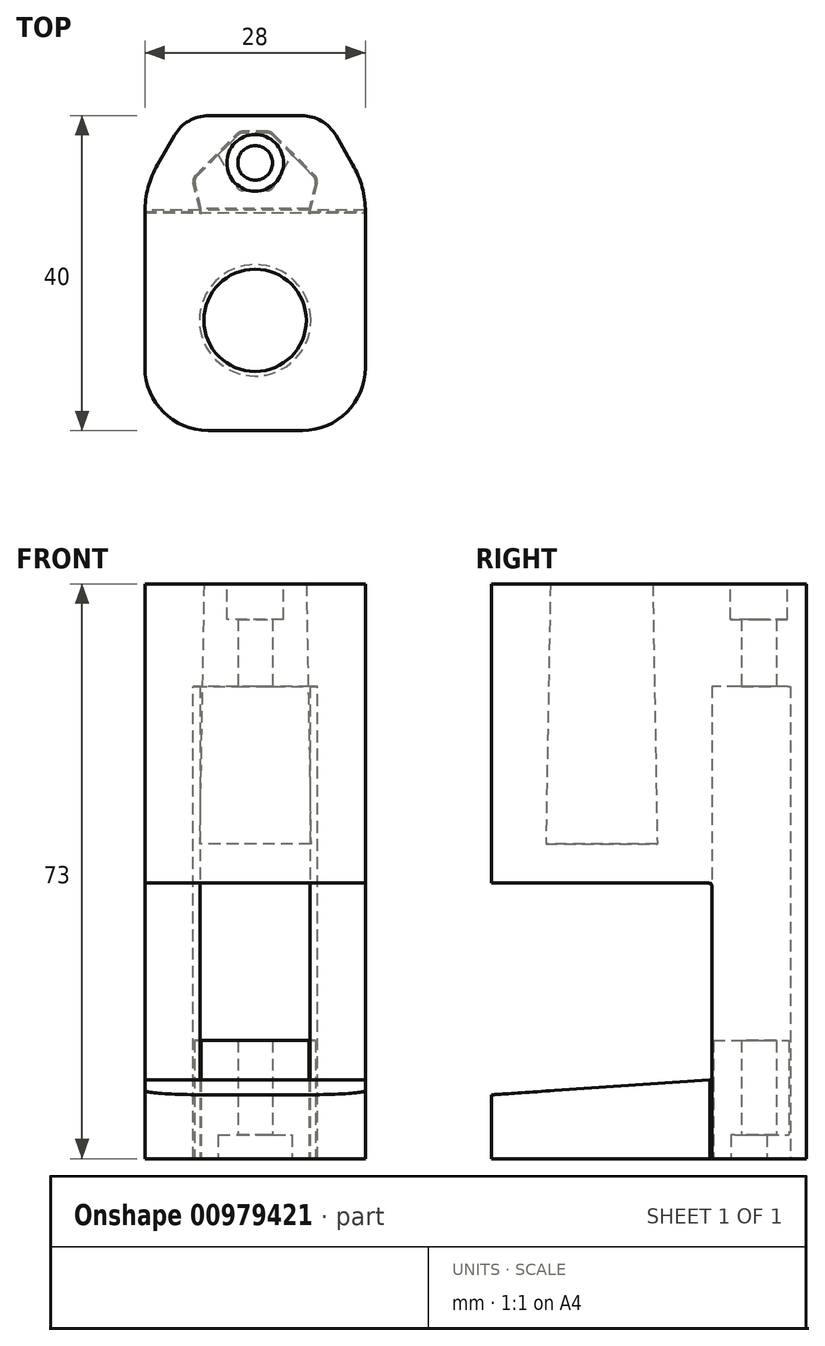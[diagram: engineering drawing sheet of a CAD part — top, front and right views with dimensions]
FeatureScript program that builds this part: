
annotation { "Feature Type Name" : "Feature", "Feature Type Description" : "" }
export const myFeature = defineFeature(function(context is Context, id is Id, definition is map)
    precondition{}
    {
        {
            assignVariable(context, id + "F0", {"name" : "lamppostDepth", "anyValue" : 33});
        }
        {
            var Q0;
            Q0=qCreatedBy(makeId("Right.planeOp"),FACE);
            var sketch = newSketch(context, id + "F1", { "sketchPlane" : qUnion([Q0])});
            skLineSegment(sketch, "E0", {"start": v(0, 0) * mm, "end": v(-28, 0) * mm});
            skLineSegment(sketch, "E1", {"start": v(-28, 0) * mm, "end": v(-28, 38) * mm});
            skLineSegment(sketch, "E2", {"start": v(-28, 38) * mm, "end": v(12, 38) * mm});
            skLineSegment(sketch, "E3", {"start": v(12, 38) * mm, "end": v(12, -35) * mm});
            skLineSegment(sketch, "E4", {"start": v(12, -35) * mm, "end": v(0, -35) * mm});
            skLineSegment(sketch, "E5", {"start": v(0, -35) * mm, "end": v(0, 0) * mm});
            skLineSegment(sketch, "E6", {"start": v(0, -25) * mm, "end": v(-22.92, -25) * mm, "construction": true});
            skSolve(sketch);
        }
        {
            var Q0;
            Q0=qSketchRegion(id+"F1",true);
            extrude(context, id + "F2", {"entities" : qUnion([Q0]), "endBound" : BoundingType.SYMMETRIC, "depth" : 28 * mm, "offsetDistance" : 25 * mm});
        }
        {
            var Q0;
            Q0=makeQuery(id+"F2.opExtrude","SWEPT_FACE",FACE,{"disambiguationData":[OSD([sQuery(id+"F1.wireOp",EDGE,"E2")])]});
            var sketch = newSketch(context, id + "F3", { "sketchPlane" : qUnion([Q0])});
            skCircle(sketch, "E7", {"center": v(0, -14) * mm, "radius": 6.5 * mm});
            skLineSegment(sketch, "E8", {"start": v(14, -28) * mm, "end": v(-14, 0) * mm, "construction": true});
            skLineSegment(sketch, "E9", {"start": v(-14, 0) * mm, "end": v(-14, -28) * mm, "construction": true});
            skSolve(sketch);
        }
        {
            var Q0;
            Q0=qSketchRegion(id+"F3",true);
            extrude(context, id + "F4", {"entities" : qUnion([Q0]), "operationType" : NewBodyOperationType.REMOVE, "oppositeDirection" : true, "depth" : (getVariable(context, 'lamppostDepth')) * mm, "offsetDistance" : 25 * mm, "hasDraft" : true, "draftAngle" : 1 * degree});
        }
        {
            var Q0;
            Q0=makeQuery(id+"F2.opExtrude","SWEPT_FACE",FACE,{"disambiguationData":[OSD([sQuery(id+"F1.wireOp",EDGE,"E4")])]});
            var sketch = newSketch(context, id + "F5", { "sketchPlane" : qUnion([Q0])});
            skCircle(sketch, "E10", {"center": v(0, -6) * mm, "radius": 2.2 * mm});
            skLineSegment(sketch, "E11", {"start": v(-14, -12) * mm, "end": v(14, 0) * mm, "construction": true});
            skSolve(sketch);
        }
        {
            var Q0;
            Q0=qSketchRegion(id+"F5",true);
            extrude(context, id + "F6", {"entities" : qUnion([Q0]), "operationType" : NewBodyOperationType.REMOVE, "endBound" : BoundingType.THROUGH_ALL, "oppositeDirection" : true, "depth" : 25 * mm, "offsetDistance" : 25 * mm});
        }
        {
            var Q0;
            Q0=makeQuery(id+"F2.opExtrude","SWEPT_FACE",FACE,{"disambiguationData":[OSD([sQuery(id+"F1.wireOp",EDGE,"E2")])]});
            var sketch = newSketch(context, id + "F7", { "sketchPlane" : qUnion([Q0])});
            skCircle(sketch, "E12", {"center": v(0, 6) * mm, "radius": 3.6 * mm});
            skSolve(sketch);
        }
        {
            var Q0;
            Q0=qSketchRegion(id+"F7",true);
            extrude(context, id + "F8", {"entities" : qUnion([Q0]), "operationType" : NewBodyOperationType.REMOVE, "oppositeDirection" : true, "depth" : 4.5 * mm, "offsetDistance" : 25 * mm});
        }
        {
            var Q0;
            Q0=makeQuery(id+"F2.opExtrude","SWEPT_FACE",FACE,{"disambiguationData":[OSD([sQuery(id+"F1.wireOp",EDGE,"E4")])]});
            var sketch = newSketch(context, id + "F9", { "sketchPlane" : qUnion([Q0])});
            skLineSegment(sketch, "E13", {"start": v(2, -10) * mm, "end": v(-2, -10) * mm});
            skPoint(sketch, "E14", {"position": v(0, -6) * mm});
            skLineSegment(sketch, "E15", {"start": v(0, -6) * mm, "end": v(0, -10) * mm, "construction": true});
            skLineSegment(sketch, "E16", {"start": v(2, -10) * mm, "end": v(8, -4) * mm});
            skLineSegment(sketch, "E17", {"start": v(8, -4) * mm, "end": v(7, 0) * mm});
            skLineSegment(sketch, "E18", {"start": v(7, 0) * mm, "end": v(-7, 0) * mm});
            skLineSegment(sketch, "E19", {"start": v(-7, 0) * mm, "end": v(-8, -4) * mm});
            skLineSegment(sketch, "E20", {"start": v(-8, -4) * mm, "end": v(-2, -10) * mm});
            skSolve(sketch);
        }
        {
            var Q0;
            Q0=qSketchRegion(id+"F9",true);
            extrude(context, id + "F10", {"entities" : qUnion([Q0]), "operationType" : NewBodyOperationType.REMOVE, "oppositeDirection" : true, "depth" : 60 * mm, "offsetDistance" : 25 * mm});
        }
        {
            var Q0;
            Q0=makeQuery(id+"F2.opExtrude","SWEPT_FACE",FACE,{"disambiguationData":[OSD([sQuery(id+"F1.wireOp",EDGE,"E4")])]});
            var sketch = newSketch(context, id + "F11", { "sketchPlane" : qUnion([Q0])});
            skLineSegment(sketch, "E21.0", {"start": v(7.78, -3.94) * mm, "end": v(6.84, -0.2) * mm});
            skLineSegment(sketch, "E21.1", {"start": v(-6.84, -0.2) * mm, "end": v(-7.78, -3.94) * mm});
            skLineSegment(sketch, "E21.2", {"start": v(-7.78, -3.94) * mm, "end": v(-1.92, -9.8) * mm});
            skLineSegment(sketch, "E21.3", {"start": v(1.92, -9.8) * mm, "end": v(-1.92, -9.8) * mm});
            skLineSegment(sketch, "E21.4", {"start": v(1.92, -9.8) * mm, "end": v(7.78, -3.94) * mm});
            skLineSegment(sketch, "E22", {"start": v(6.84, -0.2) * mm, "end": v(-6.84, -0.2) * mm});
            skCircle(sketch, "E23.0", {"center": v(0, -6) * mm, "radius": 2.2 * mm});
            skSolve(sketch);
        }
        {
            var Q0;
            Q0=qSketchRegion(id+"F11",true);
            extrude(context, id + "F12", {"entities" : qUnion([Q0]), "oppositeDirection" : true, "depth" : 15 * mm, "offsetDistance" : 25 * mm});
        }
        {
            var Q0;
            Q0=makeQuery(id+"F12.opExtrude","CAP_FACE",FACE,{"disambiguationData":[OSD([sQuery(id+"F11.wireOp",EDGE,"E21.0"),sQuery(id+"F11.wireOp",EDGE,"E21.1"),sQuery(id+"F11.wireOp",EDGE,"E21.2"),sQuery(id+"F11.wireOp",EDGE,"E21.3"),sQuery(id+"F11.wireOp",EDGE,"E21.4"),sQuery(id+"F11.wireOp",EDGE,"E22"),sQuery(id+"F11.wireOp",EDGE,"E23.0")])],"isStart":true});
            var sketch = newSketch(context, id + "F13", { "sketchPlane" : qUnion([Q0])});
            skLineSegment(sketch, "E24", {"start": v(14, 28) * mm, "end": v(-14, 28) * mm});
            skLineSegment(sketch, "E25", {"start": v(-14, 28) * mm, "end": v(-14, 0.2) * mm});
            skLineSegment(sketch, "E26", {"start": v(-14, 0.2) * mm, "end": v(-6.84, 0.2) * mm});
            skLineSegment(sketch, "E27", {"start": v(-6.84, 0.2) * mm, "end": v(-6.84, -0.2) * mm});
            skLineSegment(sketch, "E28", {"start": v(-6.84, -0.2) * mm, "end": v(6.84, -0.2) * mm});
            skLineSegment(sketch, "E29", {"start": v(6.84, -0.2) * mm, "end": v(6.84, 0.2) * mm});
            skLineSegment(sketch, "E30", {"start": v(6.84, 0.2) * mm, "end": v(14, 0.2) * mm});
            skLineSegment(sketch, "E31", {"start": v(14, 0.2) * mm, "end": v(14, 28) * mm});
            skSolve(sketch);
        }
        {
            var Q0;
            Q0=makeQuery(id+"F13.imprint","IMPRINT",FACE,{"disambiguationData":[TD([[makeQuery(id+"F13.imprint","IMPRINT",EDGE,{"derivedFrom":sQuery(id+"F13.wireOp",EDGE,"E24")}),1.0]])]});
            var Q1;
            Q1=sQuery(id+"F1.wireOp",VERTEX,"E6.end");
            extrude(context, id + "F14", {"entities" : qUnion([Q0]), "operationType" : NewBodyOperationType.ADD, "endBound" : BoundingType.UP_TO_VERTEX, "oppositeDirection" : true, "depth" : 10 * mm, "endBoundEntityVertex" : qUnion([Q1]), "offsetDistance" : 25 * mm});
        }
        {
            var Q0;
            Q0=makeQuery(id+"F14.boolean.opBoolean","MERGE",FACE,{"derivedFrom":[makeQuery(id+"F12.opExtrude","CAP_FACE",FACE,{"disambiguationData":[OSD([sQuery(id+"F11.wireOp",EDGE,"E21.0"),sQuery(id+"F11.wireOp",EDGE,"E21.1"),sQuery(id+"F11.wireOp",EDGE,"E21.2"),sQuery(id+"F11.wireOp",EDGE,"E21.3"),sQuery(id+"F11.wireOp",EDGE,"E21.4"),sQuery(id+"F11.wireOp",EDGE,"E22"),sQuery(id+"F11.wireOp",EDGE,"E23.0")])],"isStart":true}),makeQuery(id+"F14.opExtrude","CAP_FACE",FACE,{"disambiguationData":[OSD([sQuery(id+"F13.wireOp",EDGE,"E24"),sQuery(id+"F13.wireOp",EDGE,"E25"),sQuery(id+"F13.wireOp",EDGE,"E26"),sQuery(id+"F13.wireOp",EDGE,"E27"),sQuery(id+"F13.wireOp",EDGE,"E28"),sQuery(id+"F13.wireOp",EDGE,"E29"),sQuery(id+"F13.wireOp",EDGE,"E30"),sQuery(id+"F13.wireOp",EDGE,"E31")])],"isStart":true})]});
            var sketch = newSketch(context, id + "F15", { "sketchPlane" : qUnion([Q0])});
            skCircle(sketch, "E32", {"center": v(0, -6) * mm, "radius": 4.1 * mm, "construction": true});
            skLineSegment(sketch, "E33", {"start": v(2.05, -2.45) * mm, "end": v(-2.05, -2.45) * mm});
            skLineSegment(sketch, "E34", {"start": v(2.05, -2.45) * mm, "end": v(4.1, -6) * mm});
            skLineSegment(sketch, "E35", {"start": v(4.1, -6) * mm, "end": v(0, -6) * mm, "construction": true});
            skLineSegment(sketch, "E36", {"start": v(0, -6) * mm, "end": v(-4.1, -6) * mm, "construction": true});
            skLineSegment(sketch, "E37", {"start": v(-4.1, -6) * mm, "end": v(-2.05, -2.45) * mm});
            skLineSegment(sketch, "E38", {"start": v(4.1, -6) * mm, "end": v(4.7, -7.03) * mm});
            skLineSegment(sketch, "E39", {"start": v(4.7, -7.03) * mm, "end": v(1.92, -9.8) * mm});
            skLineSegment(sketch, "E40", {"start": v(1.92, -9.8) * mm, "end": v(-1.92, -9.8) * mm});
            skLineSegment(sketch, "E41", {"start": v(-1.92, -9.8) * mm, "end": v(-4.7, -7.03) * mm});
            skLineSegment(sketch, "E42", {"start": v(-4.7, -7.03) * mm, "end": v(-4.1, -6) * mm});
            skSolve(sketch);
        }
        {
            var Q0;
            Q0=qSketchRegion(id+"F15",true);
            extrude(context, id + "F16", {"entities" : qUnion([Q0]), "operationType" : NewBodyOperationType.REMOVE, "oppositeDirection" : true, "depth" : 3 * mm, "offsetDistance" : 25 * mm});
        }
        {
            var Q0;
            Q0=makeQuery(id+"F2.opExtrude","CAP_EDGE",EDGE,{"disambiguationData":[OSD([sQuery(id+"F1.wireOp",EDGE,"E1")])],"isStart":false});
            var Q1;
            Q1=makeQuery(id+"F2.opExtrude","CAP_EDGE",EDGE,{"disambiguationData":[OSD([sQuery(id+"F1.wireOp",EDGE,"E1")])],"isStart":true});
            var Q2;
            Q2=makeQuery(id+"F14.opExtrude","SWEPT_EDGE",EDGE,{"disambiguationData":[OSD([sQuery(id+"F13.wireOp",EDGE,"E24"),sQuery(id+"F13.wireOp",EDGE,"E31")])]});
            var Q3;
            Q3=makeQuery(id+"F14.opExtrude","SWEPT_EDGE",EDGE,{"disambiguationData":[OSD([sQuery(id+"F13.wireOp",EDGE,"E24"),sQuery(id+"F13.wireOp",EDGE,"E25")])]});
            fillet(context, id + "F17", {"entities" : qUnion([Q0, Q1, Q2, Q3]), "radius" : 8 * mm, "tangentPropagation" : true, "allowEdgeOverflow" : false});
        }
        {
            var Q0;
            Q0=makeQuery(id+"F2.opExtrude","CAP_EDGE",EDGE,{"disambiguationData":[OSD([sQuery(id+"F1.wireOp",EDGE,"E3")])],"isStart":true});
            var Q1;
            Q1=makeQuery(id+"F2.opExtrude","CAP_EDGE",EDGE,{"disambiguationData":[OSD([sQuery(id+"F1.wireOp",EDGE,"E3")])],"isStart":false});
            chamfer(context, id + "F18", {"entities" : qUnion([Q0, Q1]), "chamferType" : ChamferType.OFFSET_ANGLE, "width" : 9 * mm, "oppositeDirection" : false, "angle" : 30 * degree, "tangentPropagation" : true});
        }
        {
            var Q0;
            {var subQ0=sQuery(id+"F1.wireOp",EDGE,"E3");Q0=makeQuery(id+"F18.opChamfer","BLEND_EDGE",EDGE,{"blendedFrom":[makeQuery(id+"F2.opExtrude","CAP_EDGE",EDGE,{"disambiguationData":[OSD([subQ0])],"isStart":true}),makeQuery(id+"F2.opExtrude","CAP_FACE",FACE,{"disambiguationData":[OSD([sQuery(id+"F1.wireOp",EDGE,"E0"),sQuery(id+"F1.wireOp",EDGE,"E1"),sQuery(id+"F1.wireOp",EDGE,"E2"),subQ0,sQuery(id+"F1.wireOp",EDGE,"E4"),sQuery(id+"F1.wireOp",EDGE,"E5")])],"isStart":true})],"blendedInto":[makeQuery(id+"F2.opExtrude","CAP_FACE",FACE,{"disambiguationData":[OSD([sQuery(id+"F1.wireOp",EDGE,"E0"),sQuery(id+"F1.wireOp",EDGE,"E1"),sQuery(id+"F1.wireOp",EDGE,"E2"),subQ0,sQuery(id+"F1.wireOp",EDGE,"E4"),sQuery(id+"F1.wireOp",EDGE,"E5")])],"isStart":true})]});}
            var Q1;
            {var subQ0=sQuery(id+"F1.wireOp",EDGE,"E3");Q1=makeQuery(id+"F18.opChamfer","BLEND_EDGE",EDGE,{"blendedFrom":[makeQuery(id+"F2.opExtrude","CAP_EDGE",EDGE,{"disambiguationData":[OSD([subQ0])],"isStart":false}),makeQuery(id+"F2.opExtrude","CAP_FACE",FACE,{"disambiguationData":[OSD([sQuery(id+"F1.wireOp",EDGE,"E0"),sQuery(id+"F1.wireOp",EDGE,"E1"),sQuery(id+"F1.wireOp",EDGE,"E2"),subQ0,sQuery(id+"F1.wireOp",EDGE,"E4"),sQuery(id+"F1.wireOp",EDGE,"E5")])],"isStart":false})],"blendedInto":[makeQuery(id+"F2.opExtrude","CAP_FACE",FACE,{"disambiguationData":[OSD([sQuery(id+"F1.wireOp",EDGE,"E0"),sQuery(id+"F1.wireOp",EDGE,"E1"),sQuery(id+"F1.wireOp",EDGE,"E2"),subQ0,sQuery(id+"F1.wireOp",EDGE,"E4"),sQuery(id+"F1.wireOp",EDGE,"E5")])],"isStart":false})]});}
            fillet(context, id + "F19", {"entities" : qUnion([Q0, Q1]), "radius" : 12 * mm, "tangentPropagation" : true, "allowEdgeOverflow" : false});
        }
        {
            var Q0;
            {var subQ0=sQuery(id+"F1.wireOp",EDGE,"E3");Q0=makeQuery(id+"F18.opChamfer","BLEND_EDGE",EDGE,{"blendedFrom":[makeQuery(id+"F2.opExtrude","CAP_EDGE",EDGE,{"disambiguationData":[OSD([subQ0])],"isStart":true}),makeQuery(id+"F2.opExtrude","SWEPT_FACE",FACE,{"disambiguationData":[OSD([subQ0])]})],"blendedInto":[makeQuery(id+"F2.opExtrude","SWEPT_FACE",FACE,{"disambiguationData":[OSD([subQ0])]})]});}
            var Q1;
            {var subQ0=sQuery(id+"F1.wireOp",EDGE,"E3");Q1=makeQuery(id+"F18.opChamfer","BLEND_EDGE",EDGE,{"blendedFrom":[makeQuery(id+"F2.opExtrude","CAP_EDGE",EDGE,{"disambiguationData":[OSD([subQ0])],"isStart":false}),makeQuery(id+"F2.opExtrude","SWEPT_FACE",FACE,{"disambiguationData":[OSD([subQ0])]})],"blendedInto":[makeQuery(id+"F2.opExtrude","SWEPT_FACE",FACE,{"disambiguationData":[OSD([subQ0])]})]});}
            fillet(context, id + "F20", {"entities" : qUnion([Q0, Q1]), "radius" : 5 * mm, "tangentPropagation" : true, "allowEdgeOverflow" : false});
        }
        {
            var Q0;
            Q0=makeQuery(id+"F14.opExtrude","CAP_EDGE",EDGE,{"disambiguationData":[OSD([sQuery(id+"F13.wireOp",EDGE,"E28")])],"isStart":false});
            var Q1;
            {var subQ0=sQuery(id+"F1.wireOp",EDGE,"E5");var subQ1=makeQuery(id+"F2.opExtrude","SWEPT_FACE",FACE,{"disambiguationData":[OSD([subQ0])]});var subQ2=sQuery(id+"F1.wireOp",EDGE,"E0");var subQ3=makeQuery(id+"F2.opExtrude","SWEPT_FACE",FACE,{"disambiguationData":[OSD([subQ2])]});Q1=makeQuery(id+"F10.boolean.opBoolean","SPLIT",EDGE,{"disambiguationData":[topologyDisambiguationEdgeConnected([subQ3,subQ1]),TD([makeQuery(id+"F10.opExtrude","SWEPT_FACE",FACE,{"disambiguationData":[OSD([sQuery(id+"F9.wireOp",EDGE,"E17")])]})])],"derivedFrom":makeQuery(id+"F2.opExtrude","SWEPT_EDGE",EDGE,{"disambiguationData":[OSD([subQ2,subQ0])]})});}
            var Q2;
            {var subQ0=sQuery(id+"F1.wireOp",EDGE,"E5");var subQ1=makeQuery(id+"F2.opExtrude","SWEPT_FACE",FACE,{"disambiguationData":[OSD([subQ0])]});var subQ2=sQuery(id+"F1.wireOp",EDGE,"E0");var subQ3=makeQuery(id+"F2.opExtrude","SWEPT_FACE",FACE,{"disambiguationData":[OSD([subQ2])]});Q2=makeQuery(id+"F10.boolean.opBoolean","SPLIT",EDGE,{"disambiguationData":[topologyDisambiguationEdgeConnected([subQ3,subQ1]),TD([makeQuery(id+"F10.opExtrude","SWEPT_FACE",FACE,{"disambiguationData":[OSD([sQuery(id+"F9.wireOp",EDGE,"E19")])]})])],"derivedFrom":makeQuery(id+"F2.opExtrude","SWEPT_EDGE",EDGE,{"disambiguationData":[OSD([subQ2,subQ0])]})});}
            var Q3;
            Q3=makeQuery(id+"FD7lG8xIP1CFjM9_2.boolean.opBoolean","COPY",EDGE,{"derivedFrom":makeQuery(id+"FD7lG8xIP1CFjM9_2.opExtrude","SWEPT_EDGE",EDGE,{"disambiguationData":[OSD([sQuery(id+"FLmP6Xgqr9xaYfD_2.wireOp",EDGE,"iMq2RKjF-bzJq-Fhy1-qpoM-bdikvebQQUXt"),sQuery(id+"FLmP6Xgqr9xaYfD_2.wireOp",EDGE,"97yZA710-8A18-n8wI-kNBf-o7MZaln2ulbI")])]})});
            fillet(context, id + "F21", {"entities" : qUnion([Q0, Q1, Q2, Q3]), "radius" : .5 * mm, "tangentPropagation" : true, "rho" : .7, "crossSection" : FilletCrossSection.CONIC, "allowEdgeOverflow" : false});
        }
        {
            var Q0;
            Q0=makeQuery(id+"F10.boolean.opBoolean","COPY",EDGE,{"derivedFrom":makeQuery(id+"F10.opExtrude","SWEPT_EDGE",EDGE,{"disambiguationData":[OSD([sQuery(id+"F9.wireOp",EDGE,"E19"),sQuery(id+"F9.wireOp",EDGE,"E20")])]})});
            var Q1;
            Q1=makeQuery(id+"F12.opExtrude","SWEPT_EDGE",EDGE,{"disambiguationData":[OSD([sQuery(id+"F11.wireOp",EDGE,"E21.1"),sQuery(id+"F11.wireOp",EDGE,"E21.2")])]});
            var Q2;
            Q2=makeQuery(id+"F16.boolean.opBoolean","COPY",EDGE,{"derivedFrom":makeQuery(id+"F16.opExtrude","SWEPT_EDGE",EDGE,{"disambiguationData":[OSD([sQuery(id+"F15.wireOp",EDGE,"E33"),sQuery(id+"F15.wireOp",EDGE,"E37")])]})});
            var Q3;
            Q3=makeQuery(id+"F16.boolean.opBoolean","COPY",EDGE,{"derivedFrom":makeQuery(id+"F16.opExtrude","SWEPT_EDGE",EDGE,{"disambiguationData":[OSD([sQuery(id+"F15.wireOp",EDGE,"E33"),sQuery(id+"F15.wireOp",EDGE,"E34")])]})});
            var Q4;
            Q4=makeQuery(id+"F10.boolean.opBoolean","COPY",EDGE,{"derivedFrom":makeQuery(id+"F10.opExtrude","SWEPT_EDGE",EDGE,{"disambiguationData":[OSD([sQuery(id+"F9.wireOp",EDGE,"E13"),sQuery(id+"F9.wireOp",EDGE,"E20")])]})});
            var Q5;
            Q5=makeQuery(id+"F10.boolean.opBoolean","COPY",EDGE,{"derivedFrom":makeQuery(id+"F10.opExtrude","SWEPT_EDGE",EDGE,{"disambiguationData":[OSD([sQuery(id+"F9.wireOp",EDGE,"E13"),sQuery(id+"F9.wireOp",EDGE,"E16")])]})});
            var Q6;
            Q6=makeQuery(id+"F10.boolean.opBoolean","COPY",EDGE,{"derivedFrom":makeQuery(id+"F10.opExtrude","SWEPT_EDGE",EDGE,{"disambiguationData":[OSD([sQuery(id+"F9.wireOp",EDGE,"E16"),sQuery(id+"F9.wireOp",EDGE,"E17")])]})});
            var Q7;
            Q7=makeQuery(id+"F12.opExtrude","SWEPT_EDGE",EDGE,{"disambiguationData":[OSD([sQuery(id+"F11.wireOp",EDGE,"E21.0"),sQuery(id+"F11.wireOp",EDGE,"E21.4")])]});
            var Q8;
            Q8=makeQuery(id+"F12.opExtrude","SWEPT_EDGE",EDGE,{"disambiguationData":[OSD([sQuery(id+"F11.wireOp",EDGE,"E21.3"),sQuery(id+"F11.wireOp",EDGE,"E21.4")])]});
            var Q9;
            Q9=makeQuery(id+"F12.opExtrude","SWEPT_EDGE",EDGE,{"disambiguationData":[OSD([sQuery(id+"F11.wireOp",EDGE,"E21.2"),sQuery(id+"F11.wireOp",EDGE,"E21.3")])]});
            fillet(context, id + "F22", {"entities" : qUnion([Q0, Q1, Q2, Q3, Q4, Q5, Q6, Q7, Q8, Q9]), "radius" : 1 * mm, "tangentPropagation" : true, "allowEdgeOverflow" : false});
        }
        {
            var Q0;
            Q0=makeQuery(id+"F14.opExtrude","SWEPT_FACE",FACE,{"disambiguationData":[OSD([sQuery(id+"F13.wireOp",EDGE,"E31")])]});
            var sketch = newSketch(context, id + "F23", { "sketchPlane" : qUnion([Q0])});
            skLineSegment(sketch, "E43", {"start": v(-0.3, -25) * mm, "end": v(-0.3, -11.9) * mm});
            skLineSegment(sketch, "E44", {"start": v(-0.3, -11.9) * mm, "end": v(-550.31, -11.9) * mm});
            skLineSegment(sketch, "E45", {"start": v(-550.31, -11.9) * mm, "end": v(-550.31, -62.52) * mm});
            skLineSegment(sketch, "E46", {"start": v(-550.31, -62.52) * mm, "end": v(-0.3, -25) * mm});
            skSolve(sketch);
        }
        {
            var Q0;
            Q0 = qSketchRegion(id + "F23", true);
            extrude(context, id + "F24", {"entities" : qUnion([Q0]), "operationType" : NewBodyOperationType.REMOVE, "oppositeDirection" : true, "depth" : 100 * mm, "offsetDistance" : 25 * mm});
        }
    });
